# Revit family: NBS_WallgateLtd_WlHngWshBsns_SHB-05
name_source: partatom
category: Plumbing Fixtures
revit_build: Autodesk Revit 2014 (Build: 20130709_2115(x64)
units: mm (PartAtom-declared; Revit-internal decimal feet)

## types (1)
- SHB-05
    AssetType = Fixed
    BIMObjectName = NBS_WallgateLtd_WallHungWashBasins_SHB-05
    ColourOptions = MA - Thames, MAH - Frost, MAW - White, MC - Bluestone, MCA - Aubergine, MCB - Diamantina, MCC - Black, MCD - Orange, MCE - Pink, MO - Slate, MS - Hyco, MCJ - Light Grey, MCF - NHS Blue
    ConnectingDimensions = To BS EN 31
    Description = Anti-vandal solid surface basin with through wall fixings
    DrainSize = 32 mm  [stored 0.104987 ft]
    Durability = Compliant to Grade 5
    DurationUnit = year
    Features = Hygienic and easily cleaned, highly vandal-resistant
    FixingMaterial = NBS_Concept
    Form = Wall hung wash basin
    IfcExportAs = IfcSanitaryTerminalType
    IfcExportType = WASHHANDBASIN
    IntegralAccessories = Two tapholes
    IntegralAccessoryOptions = WT38 Tap Ware, BWN Deck Mounted Basin Water Nozzle, WDC Electronic Controllers, PBA Piezo Touch Buttons, PBA-IR Infra-Red Activation Sensors, WVPB Basin Water Valve Pack, MV0001 Thermostatic Mixer Valve, MBS Manifold
    ManufacturerName = Wallgate Ltd
    ManufacturerURL = www.wallgate.com
    Material = High-grade solid surface
    ModelNumber = SHB-05
    NBSCertification = www.nationalbimlibrary.com/cert/ayemhdxw
    NBSDescription = Wall hung wash basins
    NBSReference = 45-35-70/369
    Name = WallHungWashBasins_SHB-05_WallgateLtd
    NominalDepth = 380 mm
    NominalHeight = 201 mm
    NominalLength = 0 mm  [stored 0 ft]
    NominalWidth = 470 mm
    ProductInformation = www.wallgate.com/products/wash-basins/shb-basin-range
    Size = 470 x 380 x 201 mm
    Standard = BS EN 14688
    SurfaceSpreadOfFlame = Class 0 (BS 476-6), Class 1 (BS 476-7)
    Uniclass2 = 45-31-79/494
    Version = 1
    WallThicknessOptions = <150 mm
    WarrantyDurationParts = 1
    WarrantyDurationUnit = year
    WashBasinMaterial = NBS_Concept
    WashHandBasinMounting = WallHung
    WashHandBasinType = HandRinse
    Weight = 16.0 kg

note: [stored X ft] marks values corroborated as IEEE doubles in the binary element streams (Revit-internal decimal feet)

## geometry (parser evidence)
native form markers: Sweep x1
no freeform markers — native parametric forms only
